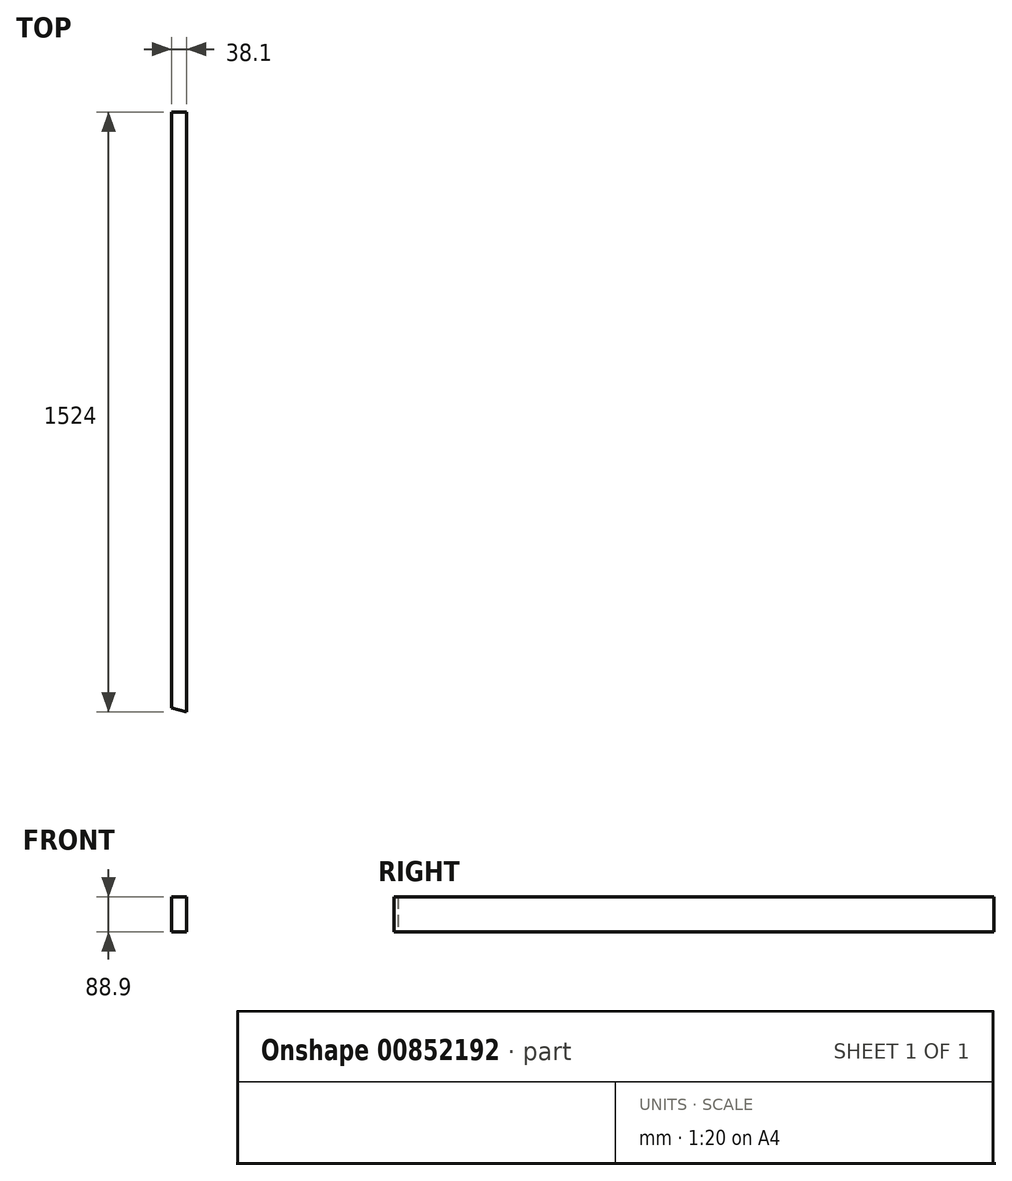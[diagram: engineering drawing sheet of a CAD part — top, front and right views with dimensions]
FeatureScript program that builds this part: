
annotation { "Feature Type Name" : "Feature", "Feature Type Description" : "" }
export const myFeature = defineFeature(function(context is Context, id is Id, definition is map)
    precondition{}
    {
        {
            var Q0;
            Q0=qCreatedBy(makeId("Front.planeOp"),FACE);
            var sketch = newSketch(context, id + "F0", { "sketchPlane" : qUnion([Q0])});
            skLineSegment(sketch, "E0.bottom", {"start": v(19.05, -44.45) * mm, "end": v(-19.05, -44.45) * mm});
            skLineSegment(sketch, "E0.top", {"start": v(19.05, 44.45) * mm, "end": v(-19.05, 44.45) * mm});
            skLineSegment(sketch, "E0.left", {"start": v(19.05, -44.45) * mm, "end": v(19.05, 44.45) * mm});
            skLineSegment(sketch, "E0.right", {"start": v(-19.05, -44.45) * mm, "end": v(-19.05, 44.45) * mm});
            skPoint(sketch, "E0.middle", {"position": v(0, 0) * mm});
            skSolve(sketch);
        }
        {
            var Q0;
            Q0=makeQuery(id+"F0.imprint","IMPRINT",FACE,{"disambiguationData":[TD([[makeQuery(id+"F0.imprint","IMPRINT",EDGE,{"derivedFrom":sQuery(id+"F0.wireOp",EDGE,"E0.bottom")}),-1.0]])]});
            extrude(context, id + "F1", {"entities" : qUnion([Q0]), "depth" : 1524 * mm, "offsetDistance" : 25.4 * mm});
        }
        {
            var Q0;
            Q0=qCreatedBy(makeId("Top.planeOp"),FACE);
            var sketch = newSketch(context, id + "F2", { "sketchPlane" : qUnion([Q0])});
            skLineSegment(sketch, "E1", {"start": v(19.05, -1524) * mm, "end": v(-19.05, -1524) * mm});
            skLineSegment(sketch, "E2", {"start": v(-19.05, -1524) * mm, "end": v(-19.05, -1513.79) * mm});
            skLineSegment(sketch, "E3", {"start": v(-19.05, -1513.79) * mm, "end": v(19.05, -1524) * mm});
            skSolve(sketch);
        }
        {
            var Q0;
            Q0=qSketchRegion(id+"F2",true);
            extrude(context, id + "F3", {"entities" : qUnion([Q0]), "operationType" : NewBodyOperationType.REMOVE, "endBound" : BoundingType.SYMMETRIC, "depth" : 127 * mm, "offsetDistance" : 25.4 * mm});
        }
    });
